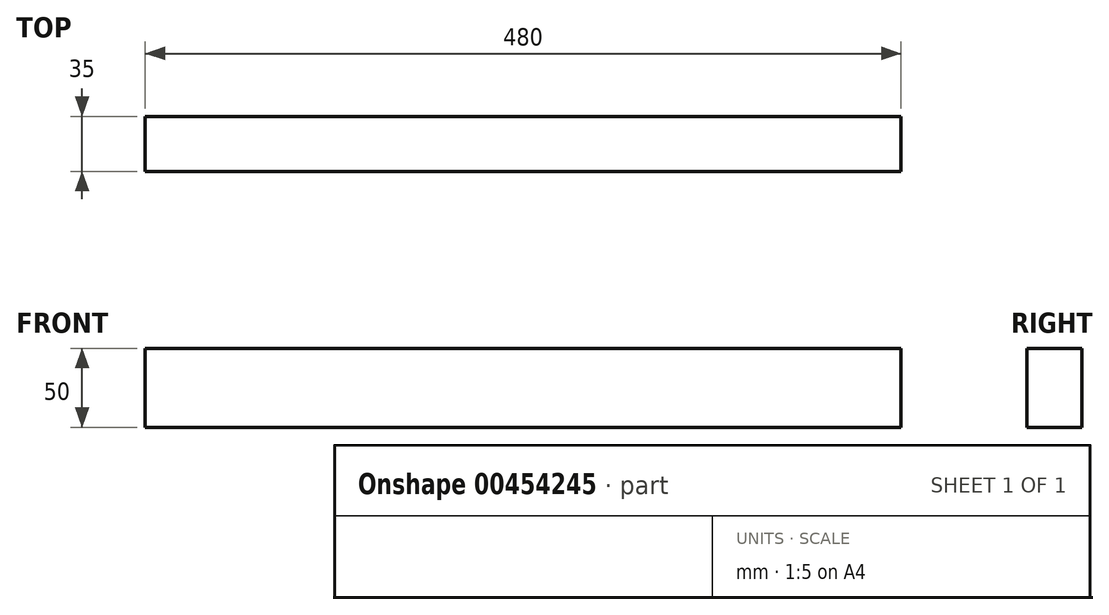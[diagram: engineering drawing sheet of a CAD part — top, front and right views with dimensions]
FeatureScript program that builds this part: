
annotation { "Feature Type Name" : "Feature", "Feature Type Description" : "" }
export const myFeature = defineFeature(function(context is Context, id is Id, definition is map)
    precondition{}
    {
        {
            var Q0;
            Q0=qCreatedBy(makeId("Front.planeOp"),FACE);
            var sketch = newSketch(context, id + "F0", { "sketchPlane" : qUnion([Q0])});
            skLineSegment(sketch, "E0.bottom", {"start": v(-240, 25) * mm, "end": v(240, 25) * mm});
            skLineSegment(sketch, "E0.top", {"start": v(-240, -25) * mm, "end": v(240, -25) * mm});
            skLineSegment(sketch, "E0.left", {"start": v(-240, 25) * mm, "end": v(-240, -25) * mm});
            skLineSegment(sketch, "E0.right", {"start": v(240, 25) * mm, "end": v(240, -25) * mm});
            skPoint(sketch, "E0.middle", {"position": v(0, 0) * mm});
            skSolve(sketch);
        }
        {
            var Q0;
            Q0=makeQuery(id+"F0.imprint","IMPRINT",FACE,{"disambiguationData":[TD([[makeQuery(id+"F0.imprint","IMPRINT",EDGE,{"derivedFrom":sQuery(id+"F0.wireOp",EDGE,"E0.bottom")}),-1.0]])]});
            extrude(context, id + "F1", {"entities" : qUnion([Q0]), "depth" : 35 * mm});
        }
    });
